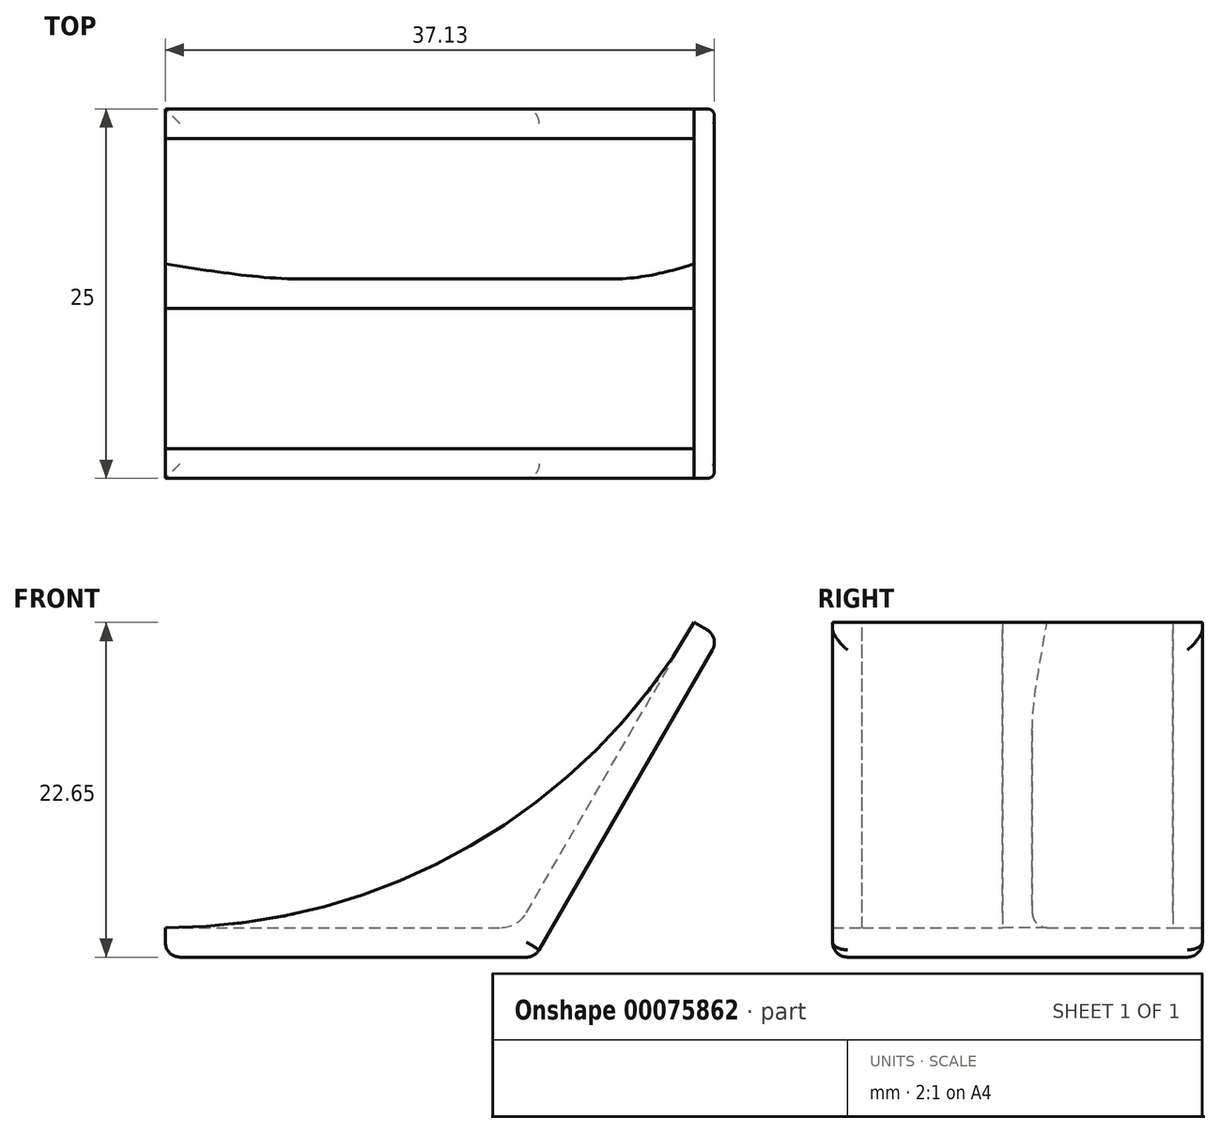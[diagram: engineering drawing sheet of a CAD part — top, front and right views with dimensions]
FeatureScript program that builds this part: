
annotation { "Feature Type Name" : "Feature", "Feature Type Description" : "" }
export const myFeature = defineFeature(function(context is Context, id is Id, definition is map)
    precondition{}
    {
        {
            var Q0;
            Q0=qCreatedBy(makeId("Front.planeOp"),FACE);
            var sketch = newSketch(context, id + "F0", { "sketchPlane" : qUnion([Q0])});
            skLineSegment(sketch, "E0", {"start": v(0, 0) * mm, "end": v(-25, 0) * mm});
            skLineSegment(sketch, "E1", {"start": v(-25, 0) * mm, "end": v(-25, 2) * mm});
            skLineSegment(sketch, "E2", {"start": v(10.77, 22.65) * mm, "end": v(12.5, 21.65) * mm});
            skLineSegment(sketch, "E3", {"start": v(12.5, 21.65) * mm, "end": v(0, 0) * mm});
            skLineSegment(sketch, "E4", {"start": v(-25, 2) * mm, "end": v(-1.15, 2) * mm});
            skLineSegment(sketch, "E5", {"start": v(-1.15, 2) * mm, "end": v(10.77, 22.65) * mm});
            skSolve(sketch);
        }
        {
            var Q0;
            Q0 = qSketchRegion(id + "F0", true);
            extrude(context, id + "F1", {"entities" : qUnion([Q0]), "depth" : 25 * mm});
        }
        {
            var Q0;
            Q0=makeQuery(id+"F1.opExtrude","CAP_FACE",FACE,{"disambiguationData":[OSD([sQuery(id+"F0.wireOp",EDGE,"E0"),sQuery(id+"F0.wireOp",EDGE,"E1"),sQuery(id+"F0.wireOp",EDGE,"E2"),sQuery(id+"F0.wireOp",EDGE,"E3"),sQuery(id+"F0.wireOp",EDGE,"E4"),sQuery(id+"F0.wireOp",EDGE,"E5")])],"isStart":true});
            var sketch = newSketch(context, id + "F2", { "sketchPlane" : qUnion([Q0])});
            skLineSegment(sketch, "E6.0", {"start": v(1.15, 2) * mm, "end": v(-10.77, 22.65) * mm});
            skLineSegment(sketch, "E7.0", {"start": v(25, 2) * mm, "end": v(1.15, 2) * mm});
            skArc(sketch, "E8", {"start": v(-10.77, 22.65) * mm, "mid": v(4.35, 7.53) * mm, "end": v(25, 2) * mm});
            skSolve(sketch);
        }
        {
            var Q0;
            Q0 = qSketchRegion(id + "F2", true);
            extrude(context, id + "F3", {"entities" : qUnion([Q0]), "operationType" : NewBodyOperationType.ADD, "oppositeDirection" : true, "depth" : 2 * mm});
        }
        {
            var Q0;
            Q0=makeQuery(id+"F1.opExtrude","CAP_FACE",FACE,{"disambiguationData":[OSD([sQuery(id+"F0.wireOp",EDGE,"E0"),sQuery(id+"F0.wireOp",EDGE,"E1"),sQuery(id+"F0.wireOp",EDGE,"E2"),sQuery(id+"F0.wireOp",EDGE,"E3"),sQuery(id+"F0.wireOp",EDGE,"E4"),sQuery(id+"F0.wireOp",EDGE,"E5")])],"isStart":false});
            var sketch = newSketch(context, id + "F4", { "sketchPlane" : qUnion([Q0])});
            skLineSegment(sketch, "E9.0", {"start": v(-1.15, 2) * mm, "end": v(10.77, 22.65) * mm});
            skLineSegment(sketch, "E10.0", {"start": v(-25, 2) * mm, "end": v(-1.15, 2) * mm});
            skArc(sketch, "E11", {"start": v(-25, 2) * mm, "mid": v(-4.35, 7.53) * mm, "end": v(10.77, 22.65) * mm});
            skSolve(sketch);
        }
        {
            var Q0;
            Q0 = qSketchRegion(id + "F4", true);
            extrude(context, id + "F5", {"entities" : qUnion([Q0]), "operationType" : NewBodyOperationType.ADD, "oppositeDirection" : true, "depth" : 2 * mm});
        }
        {
            var Q0;
            Q0=makeQuery(id+"F3.boolean.opBoolean","MERGE",FACE,{"derivedFrom":[makeQuery(id+"F1.opExtrude","CAP_FACE",FACE,{"disambiguationData":[OSD([sQuery(id+"F0.wireOp",EDGE,"E0"),sQuery(id+"F0.wireOp",EDGE,"E1"),sQuery(id+"F0.wireOp",EDGE,"E2"),sQuery(id+"F0.wireOp",EDGE,"E3"),sQuery(id+"F0.wireOp",EDGE,"E4"),sQuery(id+"F0.wireOp",EDGE,"E5")])],"isStart":true}),makeQuery(id+"F3.opExtrude","CAP_FACE",FACE,{"disambiguationData":[OSD([sQuery(id+"F2.wireOp",EDGE,"E6.0"),sQuery(id+"F2.wireOp",EDGE,"E7.0"),sQuery(id+"F2.wireOp",EDGE,"E8")])],"isStart":true})]});
            var Q1;
            Q1=makeQuery(id+"F5.boolean.opBoolean","MERGE",FACE,{"derivedFrom":[makeQuery(id+"F1.opExtrude","CAP_FACE",FACE,{"disambiguationData":[OSD([sQuery(id+"F0.wireOp",EDGE,"E0"),sQuery(id+"F0.wireOp",EDGE,"E1"),sQuery(id+"F0.wireOp",EDGE,"E2"),sQuery(id+"F0.wireOp",EDGE,"E3"),sQuery(id+"F0.wireOp",EDGE,"E4"),sQuery(id+"F0.wireOp",EDGE,"E5")])],"isStart":false}),makeQuery(id+"F5.opExtrude","CAP_FACE",FACE,{"disambiguationData":[OSD([sQuery(id+"F4.wireOp",EDGE,"E9.0"),sQuery(id+"F4.wireOp",EDGE,"E10.0"),sQuery(id+"F4.wireOp",EDGE,"E11")])],"isStart":true})]});
            cPlane(context, id + "F6", {"entities" : qUnion([Q0, Q1]), "cplaneType" : CPlaneType.MID_PLANE, "offset" : 152.4 * mm, "width" : 152.4 * mm, "height" : 152.4 * mm});
        }
        {
            var Q0;
            Q0=qCreatedBy(id+"F6.planeOp",FACE);
            var sketch = newSketch(context, id + "F7", { "sketchPlane" : qUnion([Q0])});
            skArc(sketch, "E12.0.0", {"start": v(-10.77, 22.65) * mm, "mid": v(4.35, 7.53) * mm, "end": v(25, 2) * mm});
            skLineSegment(sketch, "E12.0.1", {"start": v(25, 2) * mm, "end": v(1.15, 2) * mm});
            skLineSegment(sketch, "E12.0.2", {"start": v(1.15, 2) * mm, "end": v(-10.77, 22.65) * mm});
            skLineSegment(sketch, "E12.1", {"start": v(1.15, 2) * mm, "end": v(-10.77, 22.65) * mm});
            skSolve(sketch);
        }
        {
            var Q0;
            Q0 = qSketchRegion(id + "F7", true);
            extrude(context, id + "F8", {"entities" : qUnion([Q0]), "operationType" : NewBodyOperationType.ADD, "depth" : 1 * mm, "hasSecondDirection" : true, "secondDirectionOppositeDirection" : true, "secondDirectionDepth" : 1 * mm});
        }
        {
            var Q0;
            Q0=makeQuery(id+"F1.opExtrude","SWEPT_FACE",FACE,{"disambiguationData":[OSD([sQuery(id+"F0.wireOp",EDGE,"E3")])]});
            fillet(context, id + "F9", {"entities" : qUnion([Q0]), "radius" : 1 * mm, "tangentPropagation" : true, "allowEdgeOverflow" : false});
        }
        {
            var Q0;
            Q0=makeQuery(id+"F1.opExtrude","SWEPT_FACE",FACE,{"disambiguationData":[OSD([sQuery(id+"F0.wireOp",EDGE,"E0")])]});
            fillet(context, id + "F10", {"entities" : qUnion([Q0]), "radius" : 1 * mm, "tangentPropagation" : true, "allowEdgeOverflow" : false});
        }
        {
            var Q0;
            {var subQ0=sQuery(id+"F0.wireOp",EDGE,"E4");var subQ1=sQuery(id+"F0.wireOp",EDGE,"E5");Q0=makeQuery(id+"F8.boolean.opBoolean","SPLIT",EDGE,{"disambiguationData":[TD([makeQuery(id+"F3.opExtrude","CAP_FACE",FACE,{"disambiguationData":[OSD([sQuery(id+"F2.wireOp",EDGE,"E6.0"),sQuery(id+"F2.wireOp",EDGE,"E7.0"),sQuery(id+"F2.wireOp",EDGE,"E8")])],"isStart":false})])],"derivedFrom":makeQuery(id+"F1.opExtrude","SWEPT_EDGE",EDGE,{"disambiguationData":[OSD([subQ0,subQ1])]})});}
            var Q1;
            {var subQ0=sQuery(id+"F0.wireOp",EDGE,"E4");var subQ1=sQuery(id+"F0.wireOp",EDGE,"E5");Q1=makeQuery(id+"F8.boolean.opBoolean","SPLIT",EDGE,{"disambiguationData":[TD([makeQuery(id+"F5.opExtrude","CAP_FACE",FACE,{"disambiguationData":[OSD([sQuery(id+"F4.wireOp",EDGE,"E9.0"),sQuery(id+"F4.wireOp",EDGE,"E10.0"),sQuery(id+"F4.wireOp",EDGE,"E11")])],"isStart":false})])],"derivedFrom":makeQuery(id+"F1.opExtrude","SWEPT_EDGE",EDGE,{"disambiguationData":[OSD([subQ0,subQ1])]})});}
            fillet(context, id + "F11", {"entities" : qUnion([Q0, Q1]), "radius" : 2 * mm, "tangentPropagation" : true, "allowEdgeOverflow" : false});
        }
        {
            var Q0;
            Q0=makeQuery(id+"F3.opExtrude","CAP_EDGE",EDGE,{"disambiguationData":[OSD([sQuery(id+"F2.wireOp",EDGE,"E7.0")])],"isStart":false});
            var Q1;
            Q1=makeQuery(id+"F8.opExtrude","CAP_EDGE",EDGE,{"disambiguationData":[OSD([sQuery(id+"F7.wireOp",EDGE,"E12.0.1")])],"isStart":false});
            var Q2;
            Q2=makeQuery(id+"F5.opExtrude","CAP_EDGE",EDGE,{"disambiguationData":[OSD([sQuery(id+"F4.wireOp",EDGE,"E10.0")])],"isStart":false});
            var Q3;
            Q3=makeQuery(id+"F8.opExtrude","CAP_EDGE",EDGE,{"disambiguationData":[OSD([sQuery(id+"F7.wireOp",EDGE,"E12.0.1")])],"isStart":true});
            fillet(context, id + "F12", {"entities" : qUnion([Q0, Q1, Q2, Q3]), "radius" : 1 * mm, "tangentPropagation" : true, "allowEdgeOverflow" : false});
        }
    });
